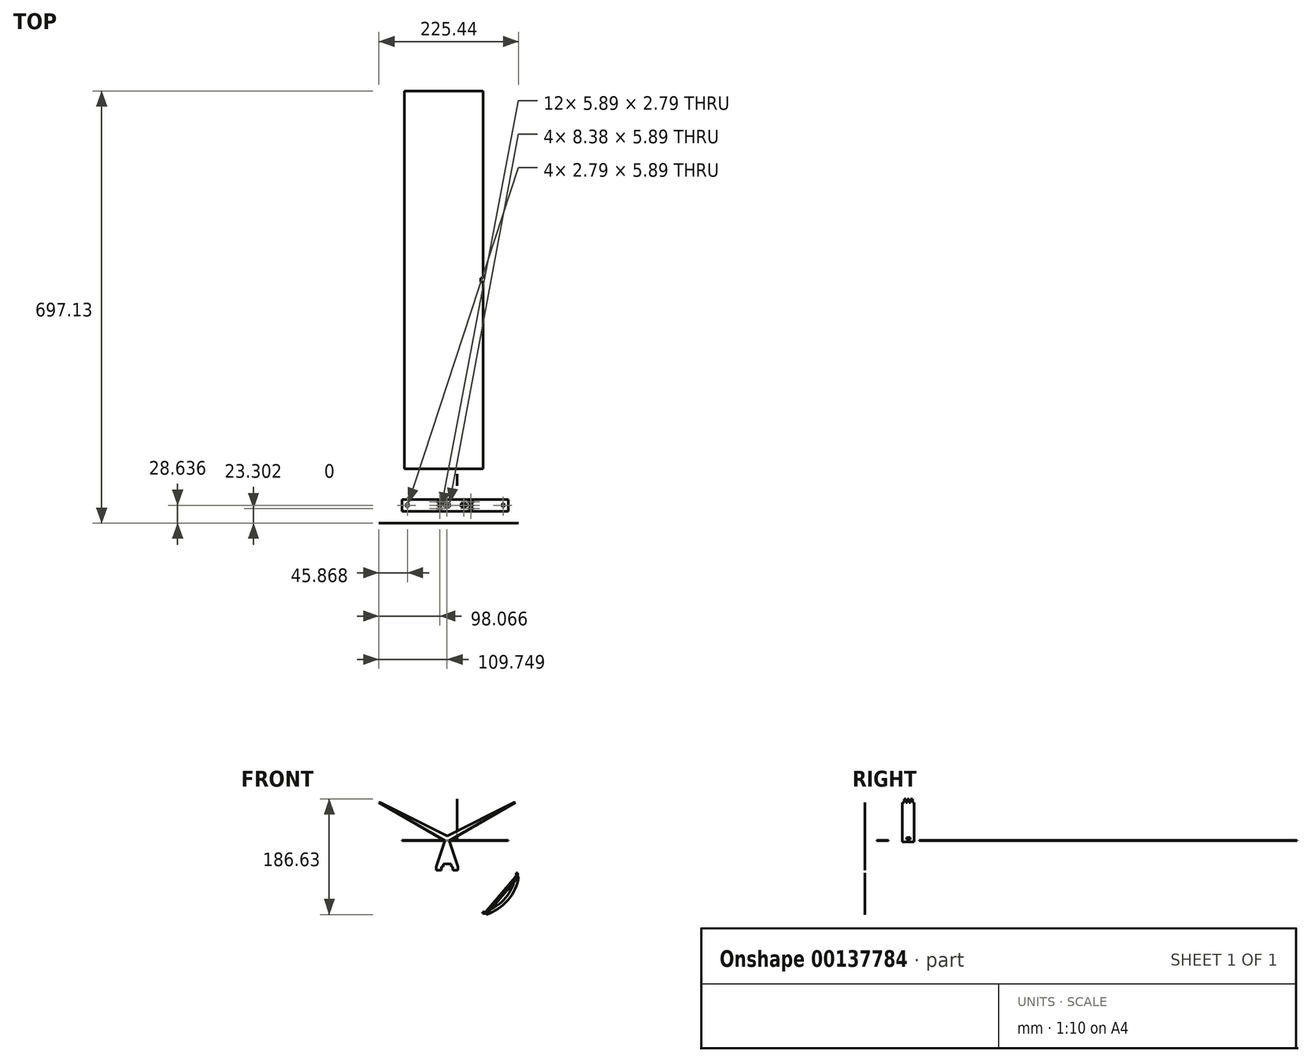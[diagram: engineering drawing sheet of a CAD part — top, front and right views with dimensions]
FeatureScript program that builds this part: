
annotation { "Feature Type Name" : "Feature", "Feature Type Description" : "" }
export const myFeature = defineFeature(function(context is Context, id is Id, definition is map)
    precondition{}
    {
        {
            assignVariable(context, id + "F0", {"name" : "WoodThickness", "anyValue" : .232});
        }
        {
            var Q0;
            Q0=qCreatedBy(makeId("Top.planeOp"),FACE);
            var sketch = newSketch(context, id + "F1", { "sketchPlane" : qUnion([Q0])});
            skLineSegment(sketch, "E0.bottom", {"start": v(-88.48, 37.93) * mm, "end": v(82.97, 37.93) * mm});
            skLineSegment(sketch, "E0.top", {"start": v(-88.48, 18.88) * mm, "end": v(82.97, 18.88) * mm});
            skLineSegment(sketch, "E0.left", {"start": v(-88.48, 37.93) * mm, "end": v(-88.48, 18.88) * mm});
            skLineSegment(sketch, "E0.right", {"start": v(82.97, 37.93) * mm, "end": v(82.97, 18.88) * mm});
            skPoint(sketch, "E1.positionSnap0", {"position": v(82.97, 28.4) * mm});
            skLineSegment(sketch, "E2.bottom", {"start": v(6.54, 31.35) * mm, "end": v(14.93, 31.35) * mm});
            skLineSegment(sketch, "E2.top", {"start": v(6.54, 25.46) * mm, "end": v(14.93, 25.46) * mm});
            skLineSegment(sketch, "E2.left", {"start": v(6.54, 31.35) * mm, "end": v(6.54, 25.46) * mm});
            skLineSegment(sketch, "E2.right", {"start": v(14.93, 31.35) * mm, "end": v(14.93, 25.46) * mm});
            skLineSegment(sketch, "E3.bottom", {"start": v(19.47, 35.14) * mm, "end": v(25.36, 35.14) * mm});
            skLineSegment(sketch, "E3.top", {"start": v(19.47, 32.34) * mm, "end": v(25.36, 32.34) * mm});
            skLineSegment(sketch, "E3.left", {"start": v(19.47, 35.14) * mm, "end": v(19.47, 32.34) * mm});
            skLineSegment(sketch, "E3.right", {"start": v(25.36, 35.14) * mm, "end": v(25.36, 32.34) * mm});
            skLineSegment(sketch, "E4.1.0.0", {"start": v(25.36, 29.8) * mm, "end": v(25.36, 27) * mm});
            skLineSegment(sketch, "E4.1.0.1", {"start": v(19.47, 29.8) * mm, "end": v(25.36, 29.8) * mm});
            skLineSegment(sketch, "E4.1.0.2", {"start": v(19.47, 27) * mm, "end": v(25.36, 27) * mm});
            skLineSegment(sketch, "E4.1.0.3", {"start": v(19.47, 29.8) * mm, "end": v(19.47, 27) * mm});
            skLineSegment(sketch, "E4.2.0.0", {"start": v(25.36, 24.47) * mm, "end": v(25.36, 21.67) * mm});
            skLineSegment(sketch, "E4.2.0.1", {"start": v(19.47, 24.47) * mm, "end": v(25.36, 24.47) * mm});
            skLineSegment(sketch, "E4.2.0.2", {"start": v(19.47, 21.67) * mm, "end": v(25.36, 21.67) * mm});
            skLineSegment(sketch, "E4.2.0.3", {"start": v(19.47, 24.47) * mm, "end": v(19.47, 21.67) * mm});
            skLineSegment(sketch, "E4.direction1", {"start": v(19.47, 32.34) * mm, "end": v(19.47, 27) * mm, "construction": true});
            skLineSegment(sketch, "E5.bottom", {"start": v(73.22, 31.35) * mm, "end": v(76.01, 31.35) * mm});
            skLineSegment(sketch, "E5.top", {"start": v(73.22, 25.46) * mm, "end": v(76.01, 25.46) * mm});
            skLineSegment(sketch, "E5.left", {"start": v(73.22, 31.35) * mm, "end": v(73.22, 25.46) * mm});
            skLineSegment(sketch, "E5.right", {"start": v(76.01, 31.35) * mm, "end": v(76.01, 25.46) * mm});
            skLineSegment(sketch, "E6", {"start": v(10.73, 31.35) * mm, "end": v(10.73, 37.93) * mm});
            skLineSegment(sketch, "E7", {"start": v(10.73, 25.46) * mm, "end": v(10.73, 18.88) * mm});
            skLineSegment(sketch, "E8", {"start": v(22.42, 35.14) * mm, "end": v(22.42, 37.93) * mm});
            skLineSegment(sketch, "E9", {"start": v(22.42, 21.67) * mm, "end": v(22.42, 18.88) * mm});
            skLineSegment(sketch, "E10", {"start": v(74.62, 31.35) * mm, "end": v(74.62, 37.93) * mm});
            skLineSegment(sketch, "E11", {"start": v(74.62, 25.46) * mm, "end": v(74.62, 18.88) * mm});
            skLineSegment(sketch, "E12", {"start": v(-2.75, 37.93) * mm, "end": v(-2.75, 18.88) * mm});
            skPoint(sketch, "E13", {"position": v(-2.75, 28.4) * mm});
            skLineSegment(sketch, "E14.MirrorCS", {"start": v(-30.87, 29.8) * mm, "end": v(-30.87, 27) * mm});
            skLineSegment(sketch, "E15.MirrorCS", {"start": v(-78.72, 31.35) * mm, "end": v(-81.52, 31.35) * mm});
            skLineSegment(sketch, "E16.MirrorCS", {"start": v(-30.87, 24.47) * mm, "end": v(-30.87, 21.67) * mm});
            skLineSegment(sketch, "E17.MirrorCS", {"start": v(-30.87, 35.14) * mm, "end": v(-30.87, 32.34) * mm});
            skLineSegment(sketch, "E18.MirrorCS", {"start": v(-24.98, 29.8) * mm, "end": v(-24.98, 27) * mm});
            skLineSegment(sketch, "E19.MirrorCS", {"start": v(-78.72, 25.46) * mm, "end": v(-81.52, 25.46) * mm});
            skLineSegment(sketch, "E20.MirrorCS", {"start": v(-24.98, 24.47) * mm, "end": v(-24.98, 21.67) * mm});
            skLineSegment(sketch, "E21.MirrorCS", {"start": v(-24.98, 35.14) * mm, "end": v(-24.98, 32.34) * mm});
            skLineSegment(sketch, "E22.MirrorCS", {"start": v(-24.98, 35.14) * mm, "end": v(-30.87, 35.14) * mm});
            skLineSegment(sketch, "E23.MirrorCS", {"start": v(-12.05, 31.35) * mm, "end": v(-12.05, 25.46) * mm});
            skLineSegment(sketch, "E24.MirrorCS", {"start": v(-24.98, 21.67) * mm, "end": v(-30.87, 21.67) * mm});
            skLineSegment(sketch, "E25.MirrorCS", {"start": v(-12.05, 25.46) * mm, "end": v(-20.43, 25.46) * mm});
            skLineSegment(sketch, "E26.MirrorCS", {"start": v(-12.05, 31.35) * mm, "end": v(-20.43, 31.35) * mm});
            skLineSegment(sketch, "E27.MirrorCS", {"start": v(-24.98, 24.47) * mm, "end": v(-30.87, 24.47) * mm});
            skLineSegment(sketch, "E28.MirrorCS", {"start": v(-24.98, 32.34) * mm, "end": v(-30.87, 32.34) * mm});
            skLineSegment(sketch, "E29.MirrorCS", {"start": v(-78.72, 31.35) * mm, "end": v(-78.72, 25.46) * mm});
            skLineSegment(sketch, "E30.MirrorCS", {"start": v(-24.98, 29.8) * mm, "end": v(-30.87, 29.8) * mm});
            skLineSegment(sketch, "E31.MirrorCS", {"start": v(-81.52, 31.35) * mm, "end": v(-81.52, 25.46) * mm});
            skLineSegment(sketch, "E32.MirrorCS", {"start": v(-20.43, 31.35) * mm, "end": v(-20.43, 25.46) * mm});
            skLineSegment(sketch, "E33.MirrorCS", {"start": v(-24.98, 27) * mm, "end": v(-30.87, 27) * mm});
            skLineSegment(sketch, "E34.MirrorCS", {"start": v(-24.98, 32.34) * mm, "end": v(-24.98, 27) * mm, "construction": true});
            skLineSegment(sketch, "E35", {"start": v(6.54, 28.4) * mm, "end": v(-2.75, 28.4) * mm});
            skLineSegment(sketch, "E36", {"start": v(-12.05, 28.4) * mm, "end": v(-2.75, 28.4) * mm});
            skLineSegment(sketch, "E37", {"start": v(25.36, 32.34) * mm, "end": v(25.36, 29.8) * mm});
            skSolve(sketch);
        }
        {
            var Q0;
            {var subQ11=sQuery(id+"F1.wireOp",EDGE,"E2.right");Q0=makeQuery(id+"F1.imprint","IMPRINT",FACE,{"disambiguationData":[TD([[makeQuery(id+"F1.imprint","IMPRINT",EDGE,{"derivedFrom":subQ11}),1.0]])]});}
            var Q1;
            {var subQ0=sQuery(id+"F1.wireOp",EDGE,"E0.left");Q1=makeQuery(id+"F1.imprint","IMPRINT",FACE,{"disambiguationData":[TD([[makeQuery(id+"F1.imprint","IMPRINT",EDGE,{"derivedFrom":subQ0}),1.0]])]});}
            var Q2;
            {var subQ3=sQuery(id+"F1.wireOp",EDGE,"E0.right");Q2=makeQuery(id+"F1.imprint","IMPRINT",FACE,{"disambiguationData":[TD([[makeQuery(id+"F1.imprint","IMPRINT",EDGE,{"derivedFrom":subQ3}),-1.0]])]});}
            var Q3;
            {var subQ0=sQuery(id+"F1.wireOp",EDGE,"E2.left");Q3=makeQuery(id+"F1.imprint","IMPRINT",FACE,{"disambiguationData":[TD([[makeQuery(id+"F1.imprint","IMPRINT",EDGE,{"derivedFrom":subQ0}),-1.0]])]});}
            var Q4;
            {var subQ15=sQuery(id+"F1.wireOp",EDGE,"E3.right");Q4=makeQuery(id+"F1.imprint","IMPRINT",FACE,{"disambiguationData":[TD([[makeQuery(id+"F1.imprint","IMPRINT",EDGE,{"derivedFrom":subQ15}),1.0]])]});}
            var Q5;
            {var subQ14=sQuery(id+"F1.wireOp",EDGE,"E4.2.0.0");Q5=makeQuery(id+"F1.imprint","IMPRINT",FACE,{"disambiguationData":[TD([[makeQuery(id+"F1.imprint","IMPRINT",EDGE,{"derivedFrom":subQ14}),1.0]])]});}
            extrude(context, id + "F2", {"entities" : qUnion([Q0, Q1, Q2, Q3, Q4, Q5]), "depth" : (getVariable(context, 'WoodThickness')) * mm});
        }
        {
            var Q0;
            Q0=qCreatedBy(makeId("Right.planeOp"),FACE);
            var sketch = newSketch(context, id + "F3", { "sketchPlane" : qUnion([Q0])});
            skLineSegment(sketch, "E38.bottom", {"start": v(79.3, -2.2) * mm, "end": v(60.25, -2.2) * mm});
            skLineSegment(sketch, "E38.top", {"start": v(79.3, 61.3) * mm, "end": v(60.25, 61.3) * mm});
            skLineSegment(sketch, "E38.left", {"start": v(79.3, -2.2) * mm, "end": v(79.3, 61.3) * mm});
            skLineSegment(sketch, "E38.right", {"start": v(60.25, -2.2) * mm, "end": v(60.25, 61.3) * mm});
            skPoint(sketch, "E38.middle", {"position": v(69.78, 29.56) * mm});
            skLineSegment(sketch, "E39.bottom", {"start": v(63.05, 61.3) * mm, "end": v(65.84, 61.3) * mm});
            skLineSegment(sketch, "E39.top", {"start": v(63.05, 67.2) * mm, "end": v(65.84, 67.2) * mm});
            skLineSegment(sketch, "E39.left", {"start": v(63.05, 61.3) * mm, "end": v(63.05, 67.2) * mm});
            skLineSegment(sketch, "E39.right", {"start": v(65.84, 61.3) * mm, "end": v(65.84, 67.2) * mm});
            skLineSegment(sketch, "E40.bottom", {"start": v(68.38, 67.2) * mm, "end": v(71.18, 67.2) * mm});
            skLineSegment(sketch, "E40.top", {"start": v(68.38, 61.3) * mm, "end": v(71.18, 61.3) * mm});
            skLineSegment(sketch, "E40.left", {"start": v(68.38, 67.2) * mm, "end": v(68.38, 61.3) * mm});
            skLineSegment(sketch, "E40.right", {"start": v(71.18, 67.2) * mm, "end": v(71.18, 61.3) * mm});
            skLineSegment(sketch, "E41.bottom", {"start": v(73.72, 67.2) * mm, "end": v(76.5, 67.2) * mm});
            skLineSegment(sketch, "E41.top", {"start": v(73.72, 61.3) * mm, "end": v(76.5, 61.3) * mm});
            skLineSegment(sketch, "E41.left", {"start": v(73.72, 67.2) * mm, "end": v(73.72, 61.3) * mm});
            skLineSegment(sketch, "E41.right", {"start": v(76.5, 67.2) * mm, "end": v(76.5, 61.3) * mm});
            skLineSegment(sketch, "E42", {"start": v(79.3, 61.3) * mm, "end": v(79.3, 54.61) * mm});
            skLineSegment(sketch, "E43", {"start": v(63.05, 61.3) * mm, "end": v(63.05, 48.35) * mm});
            skLineSegment(sketch, "E44", {"start": v(63.05, 48.35) * mm, "end": v(65.84, 48.35) * mm});
            skLineSegment(sketch, "E45", {"start": v(65.84, 48.35) * mm, "end": v(68.38, 48.35) * mm});
            skLineSegment(sketch, "E46", {"start": v(68.38, 48.35) * mm, "end": v(71.18, 48.35) * mm});
            skLineSegment(sketch, "E47", {"start": v(71.18, 48.35) * mm, "end": v(73.72, 48.35) * mm});
            skLineSegment(sketch, "E48", {"start": v(73.72, 48.35) * mm, "end": v(76.5, 48.35) * mm});
            skLineSegment(sketch, "E49", {"start": v(76.5, 48.35) * mm, "end": v(79.3, 48.35) * mm});
            skLineSegment(sketch, "E50", {"start": v(63.05, 48.35) * mm, "end": v(60.25, 48.35) * mm});
            skLineSegment(sketch, "E51", {"start": v(65.84, 61.3) * mm, "end": v(65.84, 48.35) * mm});
            skLineSegment(sketch, "E52", {"start": v(68.38, 61.3) * mm, "end": v(68.38, 48.35) * mm});
            skLineSegment(sketch, "E53", {"start": v(71.18, 61.3) * mm, "end": v(71.18, 48.35) * mm});
            skLineSegment(sketch, "E54", {"start": v(73.72, 61.3) * mm, "end": v(73.72, 48.35) * mm});
            skLineSegment(sketch, "E55", {"start": v(76.5, 61.3) * mm, "end": v(76.5, 48.35) * mm});
            skLineSegment(sketch, "E56.bottom", {"start": v(66.83, 4.57) * mm, "end": v(72.72, 4.57) * mm});
            skLineSegment(sketch, "E56.top", {"start": v(66.83, 1.78) * mm, "end": v(72.72, 1.78) * mm});
            skLineSegment(sketch, "E56.left", {"start": v(66.83, 4.57) * mm, "end": v(66.83, 1.78) * mm});
            skLineSegment(sketch, "E56.right", {"start": v(72.72, 4.57) * mm, "end": v(72.72, 1.78) * mm});
            skPoint(sketch, "E56.middle", {"position": v(69.78, 3.17) * mm});
            skLineSegment(sketch, "E57", {"start": v(72.72, 4.57) * mm, "end": v(79.3, 4.57) * mm});
            skLineSegment(sketch, "E58", {"start": v(66.83, 4.57) * mm, "end": v(60.25, 4.57) * mm});
            skSolve(sketch);
        }
        {
            var Q0;
            Q0 = qSketchRegion(id + "F3", true);
            var Q1;
            {var subQ0=sQuery(id+"F3.wireOp",EDGE,"E43");Q1=makeQuery(id+"F3.imprint","IMPRINT",FACE,{"disambiguationData":[TD([[makeQuery(id+"F3.imprint","IMPRINT",EDGE,{"derivedFrom":subQ0}),-1.0]])]});}
            var Q2;
            Q2=makeQuery(id+"F3.imprint","IMPRINT",FACE,{"disambiguationData":[TD([[makeQuery(id+"F3.imprint","IMPRINT",EDGE,{"derivedFrom":sQuery(id+"F3.wireOp",EDGE,"E40.top")}),-1.0]])]});
            var Q3;
            {var subQ0=sQuery(id+"F3.wireOp",EDGE,"E43");Q3=makeQuery(id+"F3.imprint","IMPRINT",FACE,{"disambiguationData":[TD([[makeQuery(id+"F3.imprint","IMPRINT",EDGE,{"derivedFrom":subQ0}),1.0]])]});}
            extrude(context, id + "F4", {"entities" : qUnion([Q0, Q1, Q2, Q3]), "depth" : (getVariable(context, 'WoodThickness')) * mm});
        }
        {
            var Q0;
            Q0=qCreatedBy(makeId("Front.planeOp"),FACE);
            var sketch = newSketch(context, id + "F5", { "sketchPlane" : qUnion([Q0])});
            skLineSegment(sketch, "E59", {"start": v(93.87, -58.5) * mm, "end": v(99.45, -58.5) * mm});
            skLineSegment(sketch, "E60", {"start": v(47.4, -113.84) * mm, "end": v(47.4, -119.43) * mm});
            skArc(sketch, "E61", {"start": v(47.4, -113.84) * mm, "mid": v(78.22, -92.54) * mm, "end": v(93.87, -58.5) * mm});
            skArc(sketch, "E62", {"start": v(47.4, -119.43) * mm, "mid": v(81.94, -96.23) * mm, "end": v(99.45, -58.5) * mm});
            skLineSegment(sketch, "E63.bottom", {"start": v(95.26, -52.6) * mm, "end": v(98.06, -52.6) * mm});
            skPoint(sketch, "E63.middle", {"position": v(96.66, -58.5) * mm});
            skLineSegment(sketch, "E64.left", {"start": v(41.52, -115.23) * mm, "end": v(41.52, -118.03) * mm});
            skPoint(sketch, "E64.middle", {"position": v(47.4, -116.63) * mm});
            skLineSegment(sketch, "E65", {"start": v(41.52, -115.23) * mm, "end": v(47.4, -115.23) * mm});
            skLineSegment(sketch, "E66", {"start": v(41.52, -118.03) * mm, "end": v(47.4, -118.03) * mm});
            skLineSegment(sketch, "E67", {"start": v(95.26, -52.6) * mm, "end": v(95.26, -58.5) * mm});
            skLineSegment(sketch, "E68", {"start": v(98.06, -52.6) * mm, "end": v(98.06, -58.5) * mm});
            skSolve(sketch);
        }
        {
            var Q0;
            Q0 = qSketchRegion(id + "F5", true);
            extrude(context, id + "F6", {"entities" : qUnion([Q0]), "depth" : (getVariable(context, 'WoodThickness')) * mm});
        }
        {
            var Q0;
            Q0=qCreatedBy(makeId("Front.planeOp"),FACE);
            var sketch = newSketch(context, id + "F7", { "sketchPlane" : qUnion([Q0])});
            skLineSegment(sketch, "E69.0.0", {"start": v(95.26, -58.5) * mm, "end": v(93.87, -58.5) * mm});
            skLineSegment(sketch, "E69.0.2", {"start": v(47.4, -113.84) * mm, "end": v(47.4, -115.23) * mm});
            skLineSegment(sketch, "E69.0.3", {"start": v(47.4, -115.23) * mm, "end": v(47.4, -118.03) * mm});
            skLineSegment(sketch, "E69.0.4", {"start": v(47.4, -118.03) * mm, "end": v(47.4, -119.43) * mm});
            skLineSegment(sketch, "E69.0.6", {"start": v(99.45, -58.5) * mm, "end": v(98.06, -58.5) * mm});
            skLineSegment(sketch, "E69.0.7", {"start": v(98.06, -58.5) * mm, "end": v(95.26, -58.5) * mm});
            skLineSegment(sketch, "E70.0.0", {"start": v(95.26, -52.6) * mm, "end": v(95.26, -58.5) * mm});
            skLineSegment(sketch, "E70.0.1", {"start": v(95.26, -58.5) * mm, "end": v(98.06, -58.5) * mm});
            skLineSegment(sketch, "E70.0.2", {"start": v(98.06, -58.5) * mm, "end": v(98.06, -52.6) * mm});
            skLineSegment(sketch, "E70.0.3", {"start": v(98.06, -52.6) * mm, "end": v(95.26, -52.6) * mm});
            skLineSegment(sketch, "E71.0.0", {"start": v(47.4, -118.03) * mm, "end": v(47.4, -115.23) * mm});
            skLineSegment(sketch, "E71.0.1", {"start": v(47.4, -115.23) * mm, "end": v(41.52, -115.23) * mm});
            skLineSegment(sketch, "E71.0.2", {"start": v(41.52, -115.23) * mm, "end": v(41.52, -118.03) * mm});
            skLineSegment(sketch, "E71.0.3", {"start": v(41.52, -118.03) * mm, "end": v(47.4, -118.03) * mm});
            skLineSegment(sketch, "E72", {"start": v(93.87, -58.5) * mm, "end": v(47.4, -113.84) * mm});
            skLineSegment(sketch, "E73", {"start": v(47.4, -119.43) * mm, "end": v(99.45, -58.5) * mm});
            skSolve(sketch);
        }
        {
            var Q0;
            Q0 = qSketchRegion(id + "F7", true);
            extrude(context, id + "F8", {"entities" : qUnion([Q0]), "depth" : (getVariable(context, 'WoodThickness')) * mm});
        }
        {
            var Q0;
            Q0=qCreatedBy(makeId("Front.planeOp"),FACE);
            var sketch = newSketch(context, id + "F9", { "sketchPlane" : qUnion([Q0])});
            skLineSegment(sketch, "E74", {"start": v(-126, 61.6) * mm, "end": v(-123.45, 61.6) * mm});
            skLineSegment(sketch, "E75", {"start": v(-123.45, 61.6) * mm, "end": v(-16, 7.42) * mm});
            skLineSegment(sketch, "E76", {"start": v(-16, 7.42) * mm, "end": v(91.44, 61.6) * mm});
            skLineSegment(sketch, "E77", {"start": v(91.44, 61.6) * mm, "end": v(93.98, 61.6) * mm});
            skLineSegment(sketch, "E78", {"start": v(93.98, 61.6) * mm, "end": v(-12.7, 0) * mm});
            skLineSegment(sketch, "E79", {"start": v(1.67, -47.82) * mm, "end": v(-6.71, -47.82) * mm});
            skLineSegment(sketch, "E80", {"start": v(-9.66, -37.86) * mm, "end": v(-22.36, -37.86) * mm});
            skLineSegment(sketch, "E81", {"start": v(-25.3, -47.82) * mm, "end": v(-33.68, -47.82) * mm});
            skLineSegment(sketch, "E82", {"start": v(-19.3, 0) * mm, "end": v(-126, 61.6) * mm});
            skLineSegment(sketch, "E83", {"start": v(-16, 7.42) * mm, "end": v(-16, 0) * mm});
            skLineSegment(sketch, "E84", {"start": v(-25.3, -47.82) * mm, "end": v(-25.3, -41.93) * mm});
            skLineSegment(sketch, "E85", {"start": v(-6.71, -47.82) * mm, "end": v(-6.71, -41.93) * mm});
            skLineSegment(sketch, "E86", {"start": v(-25.3, -41.93) * mm, "end": v(-22.36, -41.93) * mm});
            skLineSegment(sketch, "E87", {"start": v(-22.36, -41.93) * mm, "end": v(-22.36, -37.86) * mm});
            skLineSegment(sketch, "E88", {"start": v(-9.66, -37.86) * mm, "end": v(-9.66, -41.93) * mm});
            skLineSegment(sketch, "E89", {"start": v(-9.66, -41.93) * mm, "end": v(-6.71, -41.93) * mm});
            skLineSegment(sketch, "E90", {"start": v(-33.68, -47.82) * mm, "end": v(-33.68, -41.93) * mm});
            skLineSegment(sketch, "E91", {"start": v(-33.68, -41.93) * mm, "end": v(-19.3, 0) * mm});
            skLineSegment(sketch, "E92", {"start": v(1.67, -47.82) * mm, "end": v(1.67, -41.93) * mm});
            skLineSegment(sketch, "E93", {"start": v(1.67, -41.93) * mm, "end": v(-12.7, 0) * mm});
            skLineSegment(sketch, "E94", {"start": v(-19.3, 0) * mm, "end": v(-16, 0) * mm});
            skLineSegment(sketch, "E95", {"start": v(-12.7, 0) * mm, "end": v(-16, 0) * mm});
            skLineSegment(sketch, "E96", {"start": v(-16, -37.86) * mm, "end": v(-16, 0) * mm});
            skLineSegment(sketch, "E97", {"start": v(-19.3, 0) * mm, "end": v(-16, -1.9) * mm});
            skLineSegment(sketch, "E98", {"start": v(-12.7, 0) * mm, "end": v(-16, -1.9) * mm});
            skSolve(sketch);
        }
        {
            var Q0;
            Q0 = qSketchRegion(id + "F9", true);
            extrude(context, id + "F10", {"entities" : qUnion([Q0]), "depth" : (getVariable(context, 'WoodThickness')) * mm});
        }
        {
            var Q0;
            Q0=qCreatedBy(makeId("Front.planeOp"),FACE);
            var sketch = newSketch(context, id + "F11", { "sketchPlane" : qUnion([Q0])});
            skLineSegment(sketch, "E99.0.0", {"start": v(91.44, 61.6) * mm, "end": v(-16, 7.42) * mm});
            skLineSegment(sketch, "E99.0.1", {"start": v(-16, 7.42) * mm, "end": v(-16, 0) * mm});
            skLineSegment(sketch, "E99.0.2", {"start": v(-16, 0) * mm, "end": v(-12.7, 0) * mm});
            skLineSegment(sketch, "E99.0.3", {"start": v(-12.7, 0) * mm, "end": v(93.98, 61.6) * mm});
            skLineSegment(sketch, "E99.0.4", {"start": v(93.98, 61.6) * mm, "end": v(91.44, 61.6) * mm});
            skLineSegment(sketch, "E100.0.0", {"start": v(-123.45, 61.6) * mm, "end": v(-126, 61.6) * mm});
            skLineSegment(sketch, "E100.0.1", {"start": v(-126, 61.6) * mm, "end": v(-19.3, 0) * mm});
            skLineSegment(sketch, "E100.0.2", {"start": v(-19.3, 0) * mm, "end": v(-16, 0) * mm});
            skLineSegment(sketch, "E100.0.3", {"start": v(-16, 0) * mm, "end": v(-16, 7.42) * mm});
            skLineSegment(sketch, "E100.0.4", {"start": v(-16, 7.42) * mm, "end": v(-123.45, 61.6) * mm});
            skLineSegment(sketch, "E101.0.0", {"start": v(-16, 0) * mm, "end": v(-19.3, 0) * mm});
            skLineSegment(sketch, "E101.0.1", {"start": v(-19.3, 0) * mm, "end": v(-16, -1.9) * mm});
            skLineSegment(sketch, "E101.0.2", {"start": v(-16, -1.9) * mm, "end": v(-16, 0) * mm});
            skLineSegment(sketch, "E102.0.0", {"start": v(-16, -1.9) * mm, "end": v(-12.7, 0) * mm});
            skLineSegment(sketch, "E102.0.1", {"start": v(-12.7, 0) * mm, "end": v(-16, 0) * mm});
            skLineSegment(sketch, "E102.0.2", {"start": v(-16, 0) * mm, "end": v(-16, -1.9) * mm});
            skSolve(sketch);
        }
        {
            var Q0;
            Q0=qCreatedBy(makeId("Top.planeOp"),FACE);
            var sketch = newSketch(context, id + "F12", { "sketchPlane" : qUnion([Q0])});
            skLineSegment(sketch, "E103.bottom", {"start": v(-85.25, 696.9) * mm, "end": v(41.75, 696.9) * mm});
            skLineSegment(sketch, "E103.top", {"start": v(-85.25, 87.3) * mm, "end": v(41.75, 87.3) * mm});
            skLineSegment(sketch, "E103.left", {"start": v(-85.25, 696.9) * mm, "end": v(-85.25, 87.3) * mm});
            skLineSegment(sketch, "E103.right", {"start": v(41.75, 696.9) * mm, "end": v(41.75, 87.3) * mm});
            skLineSegment(sketch, "E104.bottom", {"start": v(37.94, 395.05) * mm, "end": v(45.56, 395.05) * mm});
            skLineSegment(sketch, "E104.top", {"start": v(37.94, 389.16) * mm, "end": v(45.56, 389.16) * mm});
            skLineSegment(sketch, "E104.left", {"start": v(37.94, 395.05) * mm, "end": v(37.94, 389.16) * mm});
            skLineSegment(sketch, "E104.right", {"start": v(45.56, 395.05) * mm, "end": v(45.56, 389.16) * mm});
            skPoint(sketch, "E104.middle", {"position": v(41.75, 392.1) * mm});
            skSolve(sketch);
        }
        {
            var Q0;
            {var subQ1=sQuery(id+"F12.wireOp",EDGE,"E103.bottom");Q0=makeQuery(id+"F12.imprint","IMPRINT",FACE,{"disambiguationData":[TD([[makeQuery(id+"F12.imprint","IMPRINT",EDGE,{"derivedFrom":subQ1}),-1.0]])]});}
            extrude(context, id + "F13", {"entities" : qUnion([Q0]), "depth" : (getVariable(context, 'WoodThickness')) * mm});
        }
    });
